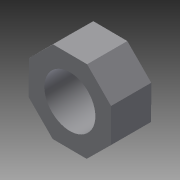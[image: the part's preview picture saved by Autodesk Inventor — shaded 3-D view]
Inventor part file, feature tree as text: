
AUTODESK INVENTOR PART (.ipt)
format: ipt  version: 2015 SP2 (Build 190223200, 223)  size: 81,920 bytes
history: native  units: mm
features: extrude x1, sketch x1
ambient origin geometry x8: Origin, YZ Plane, XZ Plane, XY Plane, X Axis, Y Axis, Z Axis, Center Point
bodies: Solid1 (feature_tree)
feature tree (2):
  extrude  "Extrusion1"  Depth=1.5mm TaperAngle=0.0deg
  sketch  "Sketch1"  dims[d0=1.9mm d1=1.5mm d2=0.0mm]
